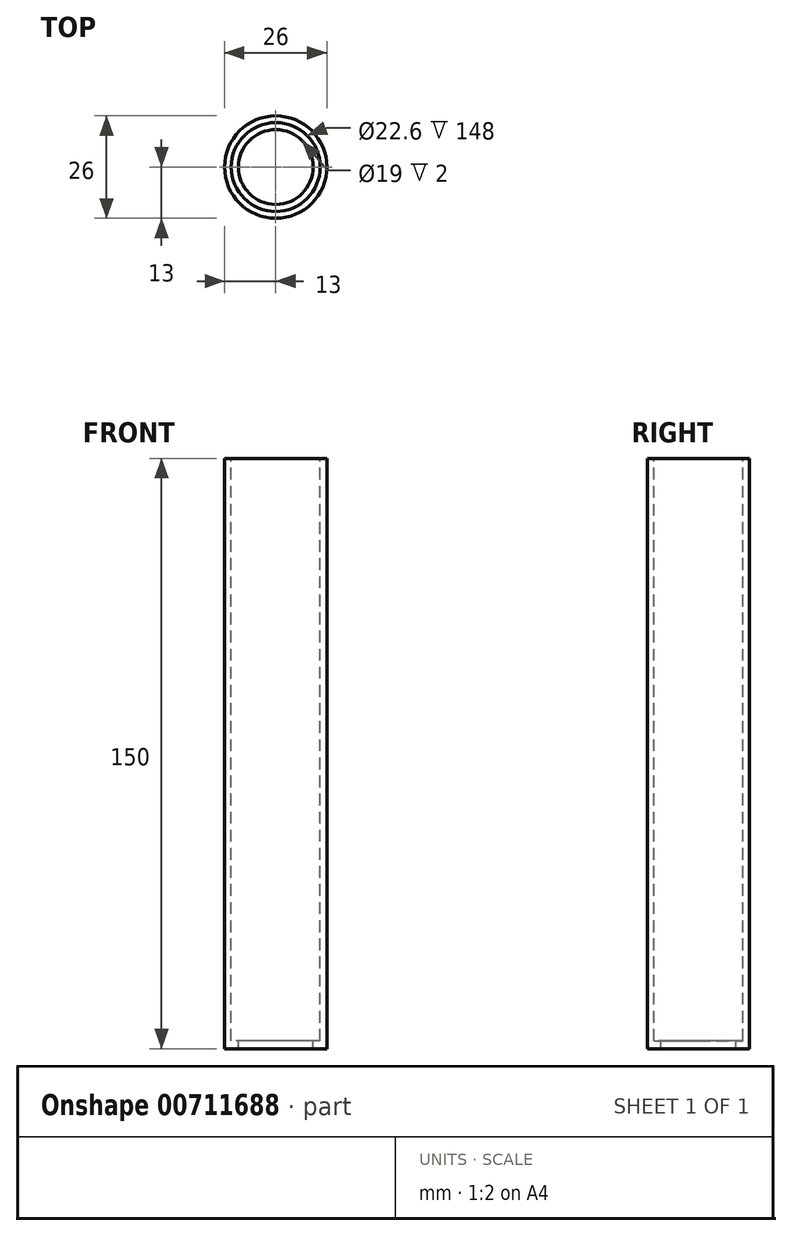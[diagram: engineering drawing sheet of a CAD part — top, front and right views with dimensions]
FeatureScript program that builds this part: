
annotation { "Feature Type Name" : "Feature", "Feature Type Description" : "" }
export const myFeature = defineFeature(function(context is Context, id is Id, definition is map)
    precondition{}
    {
        {
            var Q0;
            Q0=qCreatedBy(makeId("Top.planeOp"),FACE);
            var sketch = newSketch(context, id + "F0", { "sketchPlane" : qUnion([Q0])});
            skCircle(sketch, "E0", {"center": v(0, 0) * mm, "radius": 13 * mm});
            skSolve(sketch);
        }
        {
            var Q0;
            Q0 = qSketchRegion(id + "F0", true);
            extrude(context, id + "F1", {"entities" : qUnion([Q0]), "depth" : 150 * mm, "offsetDistance" : 25 * mm});
        }
        {
            var Q0;
            Q0=makeQuery(id+"F1.opExtrude","CAP_FACE",FACE,{"disambiguationData":[OSD([sQuery(id+"F0.wireOp",EDGE,"E0")])],"isStart":false});
            var sketch = newSketch(context, id + "F2", { "sketchPlane" : qUnion([Q0])});
            skCircle(sketch, "E1", {"center": v(0, 0) * mm, "radius": 11.3 * mm});
            skSolve(sketch);
        }
        {
            var Q0;
            Q0=makeQuery(id+"F2.imprint","IMPRINT",FACE,{"disambiguationData":[TD([[makeQuery(id+"F2.imprint","IMPRINT",EDGE,{"derivedFrom":sQuery(id+"F2.wireOp",EDGE,"E1")}),1.0]])]});
            extrude(context, id + "F3", {"entities" : qUnion([Q0]), "operationType" : NewBodyOperationType.REMOVE, "oppositeDirection" : true, "depth" : 148 * mm, "offsetDistance" : 25 * mm});
        }
        {
            var Q0;
            Q0=makeQuery(id+"F3.boolean.opBoolean","COPY",FACE,{"derivedFrom":makeQuery(id+"F3.opExtrude","CAP_FACE",FACE,{"disambiguationData":[OSD([sQuery(id+"F2.wireOp",EDGE,"E1")])],"isStart":false})});
            var sketch = newSketch(context, id + "F4", { "sketchPlane" : qUnion([Q0])});
            skCircle(sketch, "E2", {"center": v(0, 0) * mm, "radius": 9.5 * mm});
            skSolve(sketch);
        }
        {
            var Q0;
            Q0=makeQuery(id+"F4.imprint","IMPRINT",FACE,{"disambiguationData":[TD([[makeQuery(id+"F4.imprint","IMPRINT",EDGE,{"derivedFrom":sQuery(id+"F4.wireOp",EDGE,"E2")}),1.0]])]});
            extrude(context, id + "F5", {"entities" : qUnion([Q0]), "operationType" : NewBodyOperationType.REMOVE, "oppositeDirection" : true, "depth" : 2 * mm, "offsetDistance" : 25 * mm});
        }
    });
